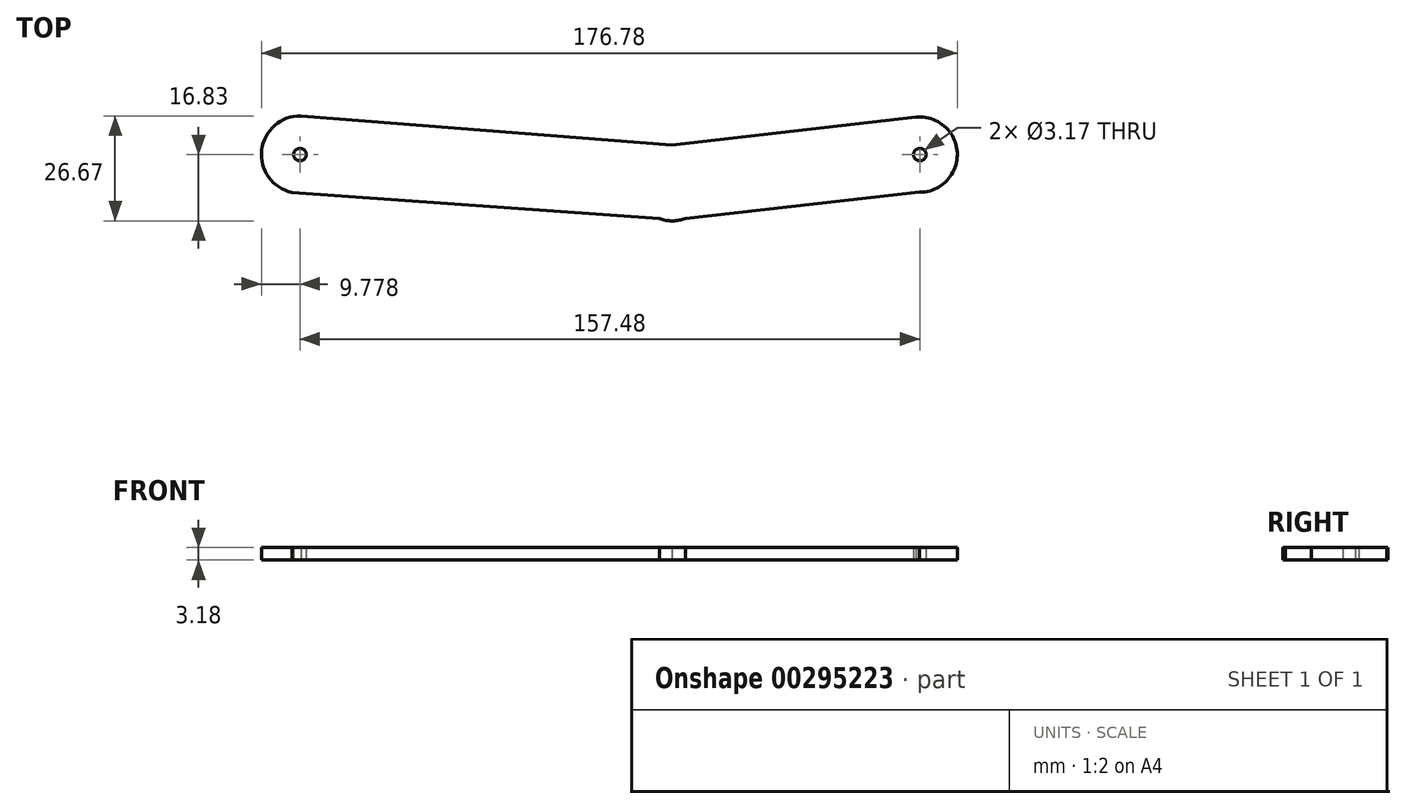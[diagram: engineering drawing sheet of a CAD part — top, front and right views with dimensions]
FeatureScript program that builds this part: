
annotation { "Feature Type Name" : "Feature", "Feature Type Description" : "" }
export const myFeature = defineFeature(function(context is Context, id is Id, definition is map)
    precondition{}
    {
        {
            var Q0;
            Q0=qCreatedBy(makeId("Top.planeOp"),FACE);
            var sketch = newSketch(context, id + "F0", { "sketchPlane" : qUnion([Q0])});
            skLineSegment(sketch, "E0", {"start": v(-94.54, 0) * mm, "end": v(62.94, 0) * mm, "construction": true});
            skCircle(sketch, "E1", {"center": v(-94.54, 0) * mm, "radius": 9.53 * mm, "construction": true});
            skCircle(sketch, "E2", {"center": v(62.94, 0) * mm, "radius": 9.53 * mm, "construction": true});
            skLineSegment(sketch, "E3", {"start": v(0, 0) * mm, "end": v(0, -7.62) * mm, "construction": true});
            skCircle(sketch, "E4", {"center": v(0, -7.62) * mm, "radius": 9.53 * mm, "construction": true});
            skLineSegment(sketch, "E5", {"start": v(-93.8, 9.5) * mm, "end": v(0, 2.08) * mm, "construction": true});
            skLineSegment(sketch, "E6", {"start": v(0, 2.08) * mm, "end": v(61.8, 9.46) * mm, "construction": true});
            skLineSegment(sketch, "E7", {"start": v(-96.75, -9.27) * mm, "end": v(-3.41, -16.51) * mm, "construction": true});
            skLineSegment(sketch, "E8", {"start": v(3.27, -16.57) * mm, "end": v(62.62, -9.52) * mm, "construction": true});
            skSolve(sketch);
        }
        {
            var Q0;
            Q0=qCreatedBy(makeId("Top.planeOp"),FACE);
            var sketch = newSketch(context, id + "F1", { "sketchPlane" : qUnion([Q0])});
            skArc(sketch, "E9", {"start": v(-94.32, 9.84) * mm, "mid": v(-104.26, 1.15) * mm, "end": v(-96.6, -9.6) * mm});
            skArc(sketch, "E10", {"start": v(3.35, -16.23) * mm, "mid": v(0.08, -16.83) * mm, "end": v(-3.2, -16.28) * mm});
            skArc(sketch, "E11", {"start": v(61.9, 9.5) * mm, "mid": v(72.45, 0.5) * mm, "end": v(62.9, -9.56) * mm});
            skLineSegment(sketch, "E12", {"start": v(-94.32, 9.84) * mm, "end": v(0, 2.42) * mm});
            skLineSegment(sketch, "E13", {"start": v(0, 2.42) * mm, "end": v(61.9, 9.5) * mm});
            skLineSegment(sketch, "E14", {"start": v(62.9, -9.56) * mm, "end": v(3.35, -16.23) * mm});
            skLineSegment(sketch, "E15", {"start": v(-3.2, -16.28) * mm, "end": v(-96.6, -9.6) * mm});
            skSolve(sketch);
        }
        {
            var Q0;
            Q0=makeQuery(id+"F1.imprint","IMPRINT",FACE,{"disambiguationData":[TD([[makeQuery(id+"F1.imprint","IMPRINT",EDGE,{"derivedFrom":sQuery(id+"F1.wireOp",EDGE,"E9")}),1.0]])]});
            extrude(context, id + "F2", {"entities" : qUnion([Q0]), "depth" : 3.17 * mm});
        }
        {
            var Q0;
            Q0=sQuery(id+"F0.wireOp",VERTEX,"E1.center");
            var Q1;
            Q1=sQuery(id+"F0.wireOp",VERTEX,"E0.end");
            var Q2;
            Q2=makeQuery(id+"F2.opExtrude","SWEPT_BODY",BODY,{"disambiguationData":[OSD([sQuery(id+"F1.wireOp",EDGE,"E9"),sQuery(id+"F1.wireOp",EDGE,"E10"),sQuery(id+"F1.wireOp",EDGE,"E11"),sQuery(id+"F1.wireOp",EDGE,"E12"),sQuery(id+"F1.wireOp",EDGE,"E13"),sQuery(id+"F1.wireOp",EDGE,"E14"),sQuery(id+"F1.wireOp",EDGE,"E15")])]});
            hole(context, id + "F3", {"style" : HoleStyle.SIMPLE, "endStyle" : HoleEndStyle.THROUGH, "oppositeDirection" : true, "holeDiameter" : 3.17 * mm, "tappedDepth" : 12.7 * mm, "tapClearance" : 3, "locations" : qUnion([Q0, Q1]), "scope" : qUnion([Q2])});
        }
    });
